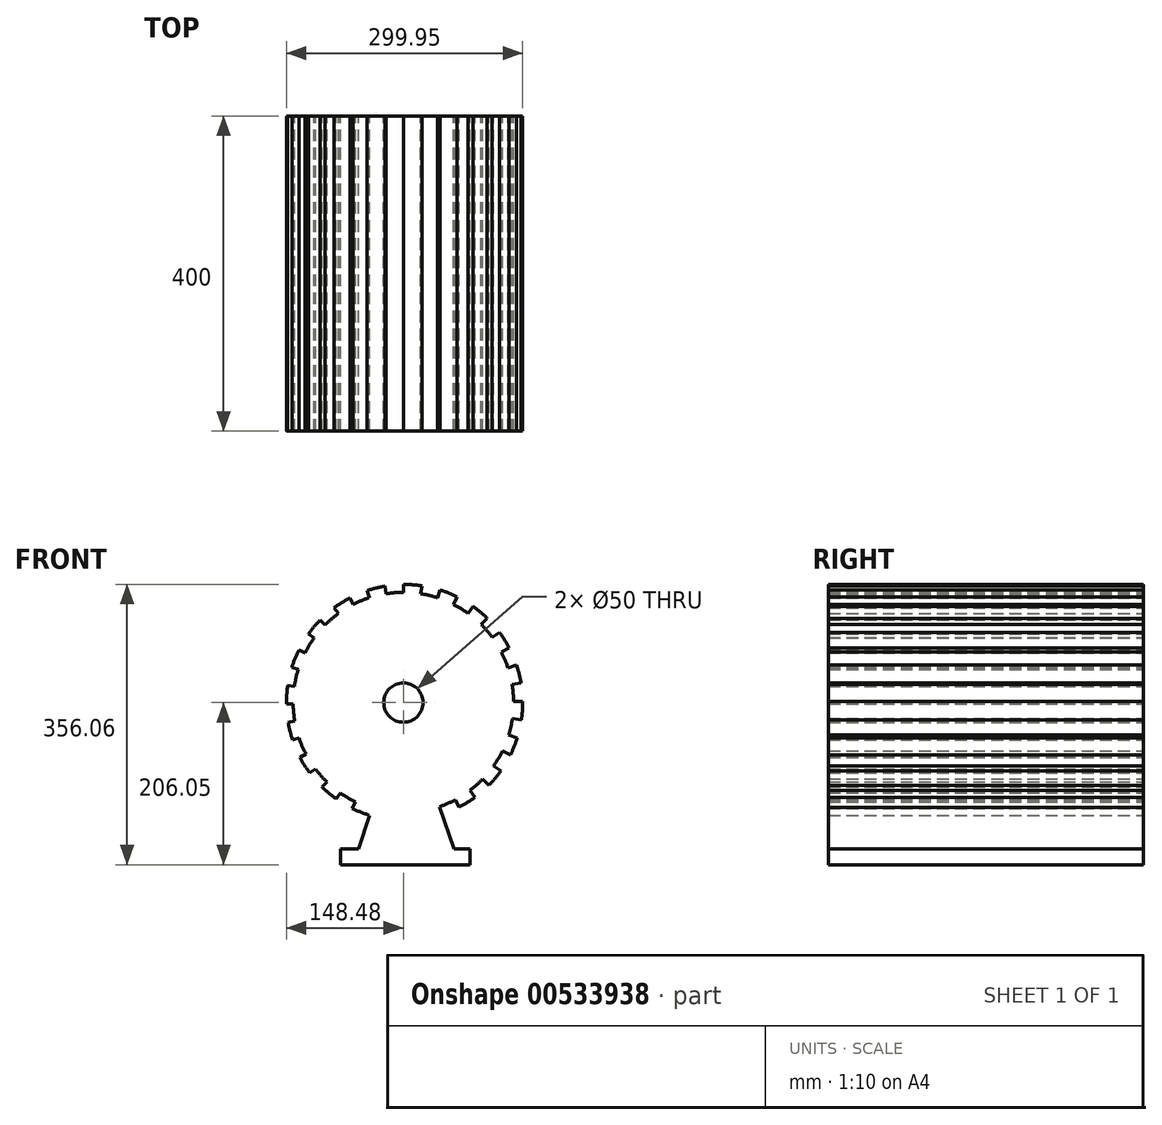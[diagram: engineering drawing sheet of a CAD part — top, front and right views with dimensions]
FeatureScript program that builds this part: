
annotation { "Feature Type Name" : "Feature", "Feature Type Description" : "" }
export const myFeature = defineFeature(function(context is Context, id is Id, definition is map)
    precondition{}
    {
        {
            var Q0;
            Q0=qCreatedBy(makeId("Front.planeOp"),FACE);
            var sketch = newSketch(context, id + "F0", { "sketchPlane" : qUnion([Q0])});
            skCircle(sketch, "E0", {"center": v(0, 0) * mm, "radius": 25 * mm});
            skArc(sketch, "E1.1.0", {"start": v(-67.92, 132.98) * mm, "mid": v(-78.14, 127.12) * mm, "end": v(-87.86, 120.48) * mm});
            skArc(sketch, "E1.2.0", {"start": v(-67.92, 132.98) * mm, "mid": v(-78.14, 127.12) * mm, "end": v(-87.86, 120.48) * mm});
            skLineSegment(sketch, "E2", {"start": v(0, 25) * mm, "end": v(0, 150) * mm});
            skLineSegment(sketch, "E3.1.0", {"start": v(-21.91, 138.27) * mm, "end": v(-23.44, 147.92) * mm});
            skLineSegment(sketch, "E3.2.0", {"start": v(-43.32, 133.13) * mm, "end": v(-46.27, 142.2) * mm});
            skLineSegment(sketch, "E3.3.0", {"start": v(-63.7, 124.67) * mm, "end": v(-67.92, 132.98) * mm});
            skLineSegment(sketch, "E3.4.0", {"start": v(-82.5, 113.1) * mm, "end": v(-87.86, 120.48) * mm});
            skLineSegment(sketch, "E3.5.0", {"start": v(-99.29, 98.7) * mm, "end": v(-105.6, 105.02) * mm});
            skLineSegment(sketch, "E3.6.0", {"start": v(-113.6, 81.81) * mm, "end": v(-120.71, 86.97) * mm});
            skLineSegment(sketch, "E3.7.0", {"start": v(-125.1, 62.86) * mm, "end": v(-132.8, 66.79) * mm});
            skLineSegment(sketch, "E3.8.0", {"start": v(-133.45, 42.31) * mm, "end": v(-141.6, 44.96) * mm});
            skLineSegment(sketch, "E3.9.0", {"start": v(-138.46, 20.69) * mm, "end": v(-146.86, 22.02) * mm});
            skLineSegment(sketch, "E3.10.0", {"start": v(-140, -1.46) * mm, "end": v(-148.48, -1.46) * mm});
            skLineSegment(sketch, "E3.11.0", {"start": v(-138, -23.57) * mm, "end": v(-146.4, -24.9) * mm});
            skLineSegment(sketch, "E3.12.0", {"start": v(-132.54, -45.09) * mm, "end": v(-140.68, -47.73) * mm});
            skLineSegment(sketch, "E3.13.0", {"start": v(-123.76, -65.46) * mm, "end": v(-131.45, -69.38) * mm});
            skLineSegment(sketch, "E3.14.0", {"start": v(-111.87, -84.17) * mm, "end": v(-118.96, -89.32) * mm});
            skLineSegment(sketch, "E3.15.0", {"start": v(-97.2, -100.76) * mm, "end": v(-103.5, -107.07) * mm});
            skLineSegment(sketch, "E3.16.0", {"start": v(-80.1, -114.82) * mm, "end": v(-85.45, -122.17) * mm});
            skLineSegment(sketch, "E3.17.0", {"start": v(-61.05, -125.99) * mm, "end": v(-65.26, -134.27) * mm});
            skLineSegment(sketch, "E3.22.0", {"start": v(46.03, -132.22) * mm, "end": v(49.25, -142.14) * mm});
            skLineSegment(sketch, "E3.23.0", {"start": v(66.07, -123.43) * mm, "end": v(70.9, -132.91) * mm});
            skLineSegment(sketch, "E3.24.0", {"start": v(84.47, -111.64) * mm, "end": v(90.85, -120.42) * mm});
            skLineSegment(sketch, "E3.25.0", {"start": v(100.8, -97.16) * mm, "end": v(108.59, -104.96) * mm});
            skLineSegment(sketch, "E3.26.0", {"start": v(114.65, -80.34) * mm, "end": v(123.7, -86.91) * mm});
            skLineSegment(sketch, "E3.27.0", {"start": v(125.72, -61.6) * mm, "end": v(135.8, -66.72) * mm});
            skLineSegment(sketch, "E3.28.0", {"start": v(133.75, -41.37) * mm, "end": v(144.58, -44.9) * mm});
            skLineSegment(sketch, "E3.29.0", {"start": v(138.54, -20.16) * mm, "end": v(149.85, -21.96) * mm});
            skLineSegment(sketch, "E3.30.0", {"start": v(140, 1.52) * mm, "end": v(151.46, 1.52) * mm});
            skLineSegment(sketch, "E3.31.0", {"start": v(138.07, 23.17) * mm, "end": v(149.38, 24.96) * mm});
            skLineSegment(sketch, "E3.32.0", {"start": v(132.82, 44.27) * mm, "end": v(143.66, 47.8) * mm});
            skLineSegment(sketch, "E3.33.0", {"start": v(124.36, 64.3) * mm, "end": v(134.44, 69.44) * mm});
            skLineSegment(sketch, "E3.34.0", {"start": v(112.88, 82.8) * mm, "end": v(121.94, 89.39) * mm});
            skLineSegment(sketch, "E3.35.0", {"start": v(98.67, 99.32) * mm, "end": v(106.48, 107.13) * mm});
            skLineSegment(sketch, "E3.36.0", {"start": v(82.04, 113.44) * mm, "end": v(88.43, 122.24) * mm});
            skLineSegment(sketch, "E3.37.0", {"start": v(63.4, 124.82) * mm, "end": v(68.25, 134.33) * mm});
            skLineSegment(sketch, "E3.38.0", {"start": v(43.18, 133.17) * mm, "end": v(46.42, 143.12) * mm});
            skLineSegment(sketch, "E3.39.0", {"start": v(21.88, 138.28) * mm, "end": v(23.48, 148.39) * mm});
            skArc(sketch, "E4", {"start": v(-132.54, -45.09) * mm, "mid": v(-128.55, -55.45) * mm, "end": v(-123.76, -65.46) * mm});
            skArc(sketch, "E5.trimOffspring", {"start": v(-105.6, 105.02) * mm, "mid": v(-113.51, 96.3) * mm, "end": v(-120.71, 86.97) * mm});
            skArc(sketch, "E6.trimOffspring", {"start": v(-23.44, 147.92) * mm, "mid": v(-34.97, 145.5) * mm, "end": v(-46.27, 142.2) * mm});
            skArc(sketch, "E7.trimOffspring", {"start": v(23.48, 148.39) * mm, "mid": v(11.77, 149.65) * mm, "end": v(0, 150) * mm});
            skArc(sketch, "E8.trimOffspring", {"start": v(68.25, 134.33) * mm, "mid": v(57.5, 139.15) * mm, "end": v(46.42, 143.12) * mm});
            skArc(sketch, "E9.trimOffspring", {"start": v(106.48, 107.13) * mm, "mid": v(97.75, 115.04) * mm, "end": v(88.43, 122.24) * mm});
            skArc(sketch, "E10.trimOffspring", {"start": v(134.44, 69.44) * mm, "mid": v(128.58, 79.66) * mm, "end": v(121.94, 89.39) * mm});
            skArc(sketch, "E11.trimOffspring", {"start": v(149.38, 24.96) * mm, "mid": v(146.97, 36.5) * mm, "end": v(143.66, 47.8) * mm});
            skArc(sketch, "E12.trimOffspring", {"start": v(149.85, -21.96) * mm, "mid": v(151.11, -10.25) * mm, "end": v(151.46, 1.52) * mm});
            skPoint(sketch, "E13.orphan", {"position": v(25.7, -6.27) * mm});
            skPoint(sketch, "E14.orphan", {"position": v(26.38, -2.4) * mm});
            skPoint(sketch, "E15.orphan", {"position": v(26.46, 1.52) * mm});
            skPoint(sketch, "E16.orphan", {"position": v(25.92, 5.41) * mm});
            skPoint(sketch, "E17.orphan", {"position": v(24.78, 9.17) * mm});
            skPoint(sketch, "E18.orphan", {"position": v(23.06, 12.7) * mm});
            skPoint(sketch, "E19.orphan", {"position": v(20.81, 15.91) * mm});
            skPoint(sketch, "E20.orphan", {"position": v(18.1, 18.74) * mm});
            skPoint(sketch, "E21.orphan", {"position": v(14.96, 21.1) * mm});
            skPoint(sketch, "E22.orphan", {"position": v(11.5, 22.96) * mm});
            skPoint(sketch, "E23.orphan", {"position": v(7.79, 24.24) * mm});
            skPoint(sketch, "E24.orphan", {"position": v(3.92, 24.93) * mm});
            skPoint(sketch, "E25.orphan", {"position": v(-3.89, 24.46) * mm});
            skPoint(sketch, "E26.orphan", {"position": v(-7.64, 23.32) * mm});
            skPoint(sketch, "E27.orphan", {"position": v(-11.17, 21.6) * mm});
            skPoint(sketch, "E28.orphan", {"position": v(-14.4, 19.36) * mm});
            skPoint(sketch, "E29.orphan", {"position": v(-17.22, 16.63) * mm});
            skPoint(sketch, "E30.orphan", {"position": v(-19.58, 13.5) * mm});
            skArc(sketch, "E31.trimOffspring", {"start": v(135.8, -66.72) * mm, "mid": v(140.61, -55.98) * mm, "end": v(144.58, -44.9) * mm});
            skPoint(sketch, "E32.orphan", {"position": v(24.41, -9.97) * mm});
            skPoint(sketch, "E33.orphan", {"position": v(22.57, -13.44) * mm});
            skPoint(sketch, "E34.orphan", {"position": v(20.2, -16.57) * mm});
            skPoint(sketch, "E35.orphan", {"position": v(17.37, -19.3) * mm});
            skPoint(sketch, "E36.orphan", {"position": v(14.15, -21.54) * mm});
            skPoint(sketch, "E37.orphan", {"position": v(10.62, -23.25) * mm});
            skArc(sketch, "E38.trimOffspring", {"start": v(-132.8, 66.79) * mm, "mid": v(-137.63, 56.04) * mm, "end": v(-141.6, 44.96) * mm});
            skArc(sketch, "E39.trimOffspring", {"start": v(-146.86, 22.02) * mm, "mid": v(-148.13, 10.31) * mm, "end": v(-148.48, -1.46) * mm});
            skArc(sketch, "E40.trimOffspring", {"start": v(-146.4, -24.9) * mm, "mid": v(-143.99, -36.43) * mm, "end": v(-140.68, -47.73) * mm});
            skArc(sketch, "E41.trimOffspring", {"start": v(-131.45, -69.38) * mm, "mid": v(-125.6, -79.6) * mm, "end": v(-118.96, -89.32) * mm});
            skPoint(sketch, "E42.orphan", {"position": v(-20.08, -12.63) * mm});
            skPoint(sketch, "E43.orphan", {"position": v(-21.8, -9.1) * mm});
            skPoint(sketch, "E44.orphan", {"position": v(-22.94, -5.35) * mm});
            skPoint(sketch, "E45.orphan", {"position": v(-23.48, -1.46) * mm});
            skPoint(sketch, "E46.orphan", {"position": v(-23.4, 2.47) * mm});
            skPoint(sketch, "E47.orphan", {"position": v(-22.72, 6.33) * mm});
            skPoint(sketch, "E48.orphan", {"position": v(-21.43, 10.04) * mm});
            skPoint(sketch, "E49.orphan", {"position": v(-17.83, -15.85) * mm});
            skPoint(sketch, "E50.orphan", {"position": v(-15.1, -18.68) * mm});
            skPoint(sketch, "E51.orphan", {"position": v(-11.98, -21.04) * mm});
            skPoint(sketch, "E52.orphan", {"position": v(-8.52, -22.9) * mm});
            skPoint(sketch, "E53.orphan", {"position": v(-4.8, -24.17) * mm});
            skPoint(sketch, "E54.orphan", {"position": v(-0.94, -24.86) * mm});
            skPoint(sketch, "E55.orphan", {"position": v(2.98, -24.94) * mm});
            skPoint(sketch, "E56.orphan", {"position": v(6.87, -24.4) * mm});
            skArc(sketch, "E57.trimOffspring", {"start": v(108.59, -104.96) * mm, "mid": v(116.5, -96.23) * mm, "end": v(123.7, -86.91) * mm});
            skArc(sketch, "E58.trimOffspring", {"start": v(-103.5, -107.07) * mm, "mid": v(-94.77, -114.97) * mm, "end": v(-85.45, -122.17) * mm});
            skArc(sketch, "E59.trimOffspring", {"start": v(70.9, -132.91) * mm, "mid": v(81.12, -127.06) * mm, "end": v(90.85, -120.42) * mm});
            skArc(sketch, "E60.trimOffspring", {"start": v(-65.26, -134.27) * mm, "mid": v(-54.47, -139.11) * mm, "end": v(-43.32, -143.1) * mm});
            skArc(sketch, "E61.trimOffspring", {"start": v(-140, -1.46) * mm, "mid": v(-139.44, -12.55) * mm, "end": v(-138, -23.57) * mm});
            skArc(sketch, "E62.trimOffspring", {"start": v(-133.45, 42.31) * mm, "mid": v(-136.39, 31.6) * mm, "end": v(-138.46, 20.69) * mm});
            skArc(sketch, "E63.trimOffspring", {"start": v(-113.6, 81.81) * mm, "mid": v(-119.73, 72.56) * mm, "end": v(-125.1, 62.86) * mm});
            skArc(sketch, "E64.trimOffspring", {"start": v(-82.5, 113.1) * mm, "mid": v(-91.18, 106.24) * mm, "end": v(-99.29, 98.7) * mm});
            skArc(sketch, "E65.trimOffspring", {"start": v(-43.32, 133.13) * mm, "mid": v(-53.67, 129.3) * mm, "end": v(-63.7, 124.67) * mm});
            skArc(sketch, "E66.trimOffspring", {"start": v(0, 140) * mm, "mid": v(-11, 139.57) * mm, "end": v(-21.91, 138.27) * mm});
            skArc(sketch, "E67.trimOffspring", {"start": v(43.18, 133.17) * mm, "mid": v(32.63, 136.14) * mm, "end": v(21.88, 138.28) * mm});
            skArc(sketch, "E68.trimOffspring", {"start": v(82.04, 113.44) * mm, "mid": v(72.94, 119.5) * mm, "end": v(63.4, 124.82) * mm});
            skArc(sketch, "E69.trimOffspring", {"start": v(112.88, 82.8) * mm, "mid": v(106.1, 91.34) * mm, "end": v(98.67, 99.32) * mm});
            skArc(sketch, "E70.trimOffspring", {"start": v(132.82, 44.27) * mm, "mid": v(128.98, 54.45) * mm, "end": v(124.36, 64.3) * mm});
            skArc(sketch, "E71.trimOffspring", {"start": v(140, 1.52) * mm, "mid": v(139.45, 12.39) * mm, "end": v(138.07, 23.17) * mm});
            skArc(sketch, "E72.trimOffspring", {"start": v(133.75, -41.37) * mm, "mid": v(136.56, -30.86) * mm, "end": v(138.54, -20.16) * mm});
            skArc(sketch, "E73.trimOffspring", {"start": v(114.65, -80.34) * mm, "mid": v(120.55, -71.18) * mm, "end": v(125.72, -61.6) * mm});
            skLineSegment(sketch, "E74.bottom", {"start": v(84.47, -206.05) * mm, "end": v(-80.1, -206.05) * mm});
            skLineSegment(sketch, "E74.top", {"start": v(84.47, -186.05) * mm, "end": v(64.6, -186.05) * mm});
            skLineSegment(sketch, "E74.left", {"start": v(84.47, -206.05) * mm, "end": v(84.47, -186.05) * mm});
            skLineSegment(sketch, "E74.right", {"start": v(-80.1, -206.05) * mm, "end": v(-80.1, -186.05) * mm});
            skArc(sketch, "E75.trimOffspring", {"start": v(-111.87, -84.17) * mm, "mid": v(-104.86, -92.76) * mm, "end": v(-97.2, -100.76) * mm});
            skArc(sketch, "E76.trimOffspring", {"start": v(84.47, -111.64) * mm, "mid": v(92.92, -104.72) * mm, "end": v(100.8, -97.16) * mm});
            skArc(sketch, "E77.trimOffspring", {"start": v(-80.1, -114.82) * mm, "mid": v(-70.8, -120.78) * mm, "end": v(-61.05, -125.99) * mm});
            skArc(sketch, "E78.trimOffspring", {"start": v(46.03, -132.22) * mm, "mid": v(56.22, -128.22) * mm, "end": v(66.07, -123.43) * mm});
            skLineSegment(sketch, "E79", {"start": v(-43.32, -143.1) * mm, "end": v(-56.7, -186.05) * mm});
            skLineSegment(sketch, "E80", {"start": v(46.03, -132.22) * mm, "end": v(64.6, -186.05) * mm});
            skLineSegment(sketch, "E81.trimOffspring", {"start": v(-56.7, -186.05) * mm, "end": v(-80.1, -186.05) * mm});
            skArc(sketch, "E82", {"start": v(-43.32, -143.1) * mm, "mid": v(2.3, -145.36) * mm, "end": v(46.03, -132.22) * mm});
            skSolve(sketch);
        }
        {
            var Q0;
            Q0 = qSketchRegion(id + "F0", true);
            extrude(context, id + "F1", {"entities" : qUnion([Q0]), "endBound" : BoundingType.SYMMETRIC, "depth" : 400 * mm, "offsetDistance" : 25 * mm});
        }
    });
